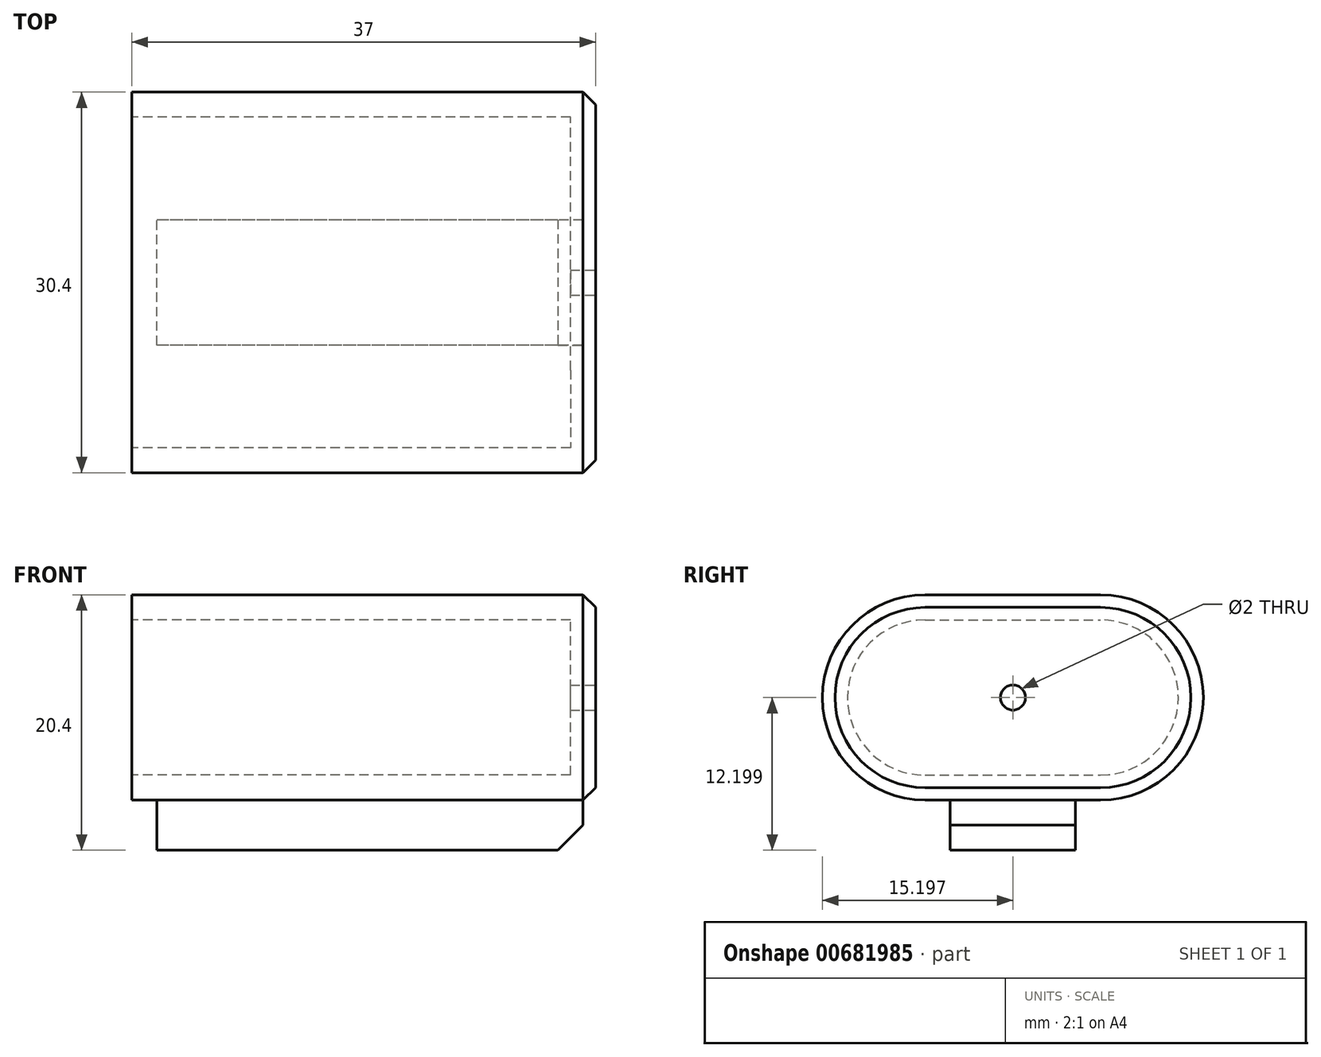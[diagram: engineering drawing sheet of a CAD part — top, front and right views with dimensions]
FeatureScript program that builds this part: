
annotation { "Feature Type Name" : "Feature", "Feature Type Description" : "" }
export const myFeature = defineFeature(function(context is Context, id is Id, definition is map)
    precondition{}
    {
        {
            var Q0;
            Q0=qCreatedBy(makeId("Right.planeOp"),FACE);
            var sketch = newSketch(context, id + "F0", { "sketchPlane" : qUnion([Q0])});
            skLineSegment(sketch, "E0.bottom", {"start": v(-2.34, -5.75) * mm, "end": v(11.66, -5.75) * mm});
            skLineSegment(sketch, "E0.top", {"start": v(-2.34, 6.65) * mm, "end": v(11.66, 6.65) * mm});
            skLineSegment(sketch, "E0.left", {"start": v(-8.54, 0.45) * mm, "end": v(-8.54, 0.45) * mm});
            skLineSegment(sketch, "E0.right", {"start": v(17.86, 0.45) * mm, "end": v(17.86, 0.45) * mm});
            skPoint(sketch, "E1.visualSharp", {"position": v(17.86, 6.65) * mm});
            skArc(sketch, "E1.filletArc", {"start": v(17.86, 0.45) * mm, "mid": v(16.04, 4.83) * mm, "end": v(11.66, 6.65) * mm});
            skPoint(sketch, "E2.visualSharp", {"position": v(17.86, -5.75) * mm});
            skArc(sketch, "E2.filletArc", {"start": v(11.66, -5.75) * mm, "mid": v(16.04, -3.94) * mm, "end": v(17.86, 0.45) * mm});
            skPoint(sketch, "E3.visualSharp", {"position": v(-8.54, 6.65) * mm});
            skArc(sketch, "E3.filletArc", {"start": v(-2.34, 6.65) * mm, "mid": v(-6.73, 4.83) * mm, "end": v(-8.54, 0.45) * mm});
            skPoint(sketch, "E4.visualSharp", {"position": v(-8.54, -5.75) * mm});
            skArc(sketch, "E4.filletArc", {"start": v(-8.54, 0.45) * mm, "mid": v(-6.73, -3.94) * mm, "end": v(-2.34, -5.75) * mm});
            skSolve(sketch);
        }
        {
            var Q0;
            Q0 = qSketchRegion(id + "F0", true);
            extrude(context, id + "F1", {"entities" : qUnion([Q0]), "depth" : 35 * mm, "offsetDistance" : 25 * mm});
        }
        {
            var Q0;
            Q0=makeQuery(id+"F1.opExtrude","CAP_FACE",FACE,{"disambiguationData":[OSD([sQuery(id+"F0.wireOp",EDGE,"E0.bottom"),sQuery(id+"F0.wireOp",EDGE,"E0.top"),sQuery(id+"F0.wireOp",EDGE,"E1.filletArc"),sQuery(id+"F0.wireOp",EDGE,"E2.filletArc"),sQuery(id+"F0.wireOp",EDGE,"E3.filletArc"),sQuery(id+"F0.wireOp",EDGE,"E4.filletArc")])],"isStart":true});
            shell(context, id + "F2", {"entities" : qUnion([Q0]), "thickness" : 2 * mm, "oppositeDirection" : true});
        }
        {
            var Q0;
            Q0=makeQuery(id+"F1.opExtrude","CAP_EDGE",EDGE,{"disambiguationData":[OSD([sQuery(id+"F0.wireOp",EDGE,"E0.top")])],"isStart":false});
            var Q1;
            Q1=makeQuery(id+"F1.opExtrude","CAP_EDGE",EDGE,{"disambiguationData":[OSD([sQuery(id+"F0.wireOp",EDGE,"E1.filletArc"),sQuery(id+"F0.wireOp",EDGE,"E2.filletArc")])],"isStart":false});
            var Q2;
            Q2=makeQuery(id+"F1.opExtrude","CAP_EDGE",EDGE,{"disambiguationData":[OSD([sQuery(id+"F0.wireOp",EDGE,"E0.bottom")])],"isStart":false});
            var Q3;
            Q3=makeQuery(id+"F1.opExtrude","CAP_EDGE",EDGE,{"disambiguationData":[OSD([sQuery(id+"F0.wireOp",EDGE,"E3.filletArc"),sQuery(id+"F0.wireOp",EDGE,"E4.filletArc")])],"isStart":false});
            chamfer(context, id + "F3", {"entities" : qUnion([Q0, Q1, Q2, Q3]), "width" : 1 * mm, "tangentPropagation" : true});
        }
        {
            var Q0;
            Q0=makeQuery(id+"F1.opExtrude","CAP_FACE",FACE,{"disambiguationData":[OSD([sQuery(id+"F0.wireOp",EDGE,"E0.bottom"),sQuery(id+"F0.wireOp",EDGE,"E0.top"),sQuery(id+"F0.wireOp",EDGE,"E1.filletArc"),sQuery(id+"F0.wireOp",EDGE,"E2.filletArc"),sQuery(id+"F0.wireOp",EDGE,"E3.filletArc"),sQuery(id+"F0.wireOp",EDGE,"E4.filletArc")])],"isStart":false});
            var sketch = newSketch(context, id + "F4", { "sketchPlane" : qUnion([Q0])});
            skCircle(sketch, "E5", {"center": v(4.66, 0.45) * mm, "radius": 1 * mm});
            skSolve(sketch);
        }
        {
            var Q0;
            Q0=makeQuery(id+"F4.imprint","IMPRINT",FACE,{"disambiguationData":[TD([[makeQuery(id+"F4.imprint","IMPRINT",EDGE,{"derivedFrom":sQuery(id+"F4.wireOp",EDGE,"E5")}),1.0]])]});
            var Q1;
            Q1=sQuery(id+"F4.wireOp",EDGE,"E5");
            extrude(context, id + "F5", {"entities" : qUnion([Q0]), "operationType" : NewBodyOperationType.REMOVE, "surfaceEntities" : qUnion([Q1]), "oppositeDirection" : true, "depth" : 3 * mm, "offsetDistance" : 25 * mm});
        }
        {
            var Q0;
            Q0=makeQuery(id+"F1.opExtrude","SWEPT_FACE",FACE,{"disambiguationData":[OSD([sQuery(id+"F0.wireOp",EDGE,"E0.bottom")])]});
            var sketch = newSketch(context, id + "F6", { "sketchPlane" : qUnion([Q0])});
            skLineSegment(sketch, "E6.bottom", {"start": v(36, 0.34) * mm, "end": v(2, 0.34) * mm});
            skLineSegment(sketch, "E6.top", {"start": v(36, -9.66) * mm, "end": v(2, -9.66) * mm});
            skLineSegment(sketch, "E6.left", {"start": v(36, 0.34) * mm, "end": v(36, -9.66) * mm});
            skLineSegment(sketch, "E6.right", {"start": v(2, 0.34) * mm, "end": v(2, -9.66) * mm});
            skSolve(sketch);
        }
        {
            var Q0;
            Q0=makeQuery(id+"F6.imprint","IMPRINT",FACE,{"disambiguationData":[TD([[makeQuery(id+"F6.imprint","IMPRINT",EDGE,{"derivedFrom":sQuery(id+"F6.wireOp",EDGE,"E6.bottom")}),1.0]])]});
            extrude(context, id + "F7", {"entities" : qUnion([Q0]), "operationType" : NewBodyOperationType.ADD, "depth" : 4 * mm, "offsetDistance" : 25 * mm});
        }
        {
            var Q0;
            Q0=makeQuery(id+"F7.opExtrude","CAP_EDGE",EDGE,{"disambiguationData":[OSD([sQuery(id+"F6.wireOp",EDGE,"E6.left")])],"isStart":false});
            chamfer(context, id + "F8", {"entities" : qUnion([Q0]), "width" : 2 * mm, "tangentPropagation" : true});
        }
    });
